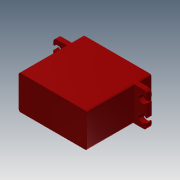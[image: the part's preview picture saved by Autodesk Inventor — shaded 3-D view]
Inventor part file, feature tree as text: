
AUTODESK INVENTOR PART (.ipt)
format: ipt  version: 2013 (Build 170138000, 138)  size: 210,432 bytes
history: native  units: mm
features: fillet x12, extrude x8, sketch x8, chamfer x1
ambient origin geometry x8: Origin, YZ Plane, XZ Plane, XY Plane, X Axis, Y Axis, Z Axis, Center Point
bodies: Solid1 (feature_tree)
feature tree (29):
  extrude  "Extrusion1"  Depth=7.4mm TaperAngle=0.0deg
  sketch  "Sketch2"  dims[d10=7.4mm d11=0.0mm d18=5.8mm d19=0.0mm]
  extrude  "Extrusion2"  Depth=5.8mm TaperAngle=0.0deg
  extrude  "Extrusion3"  Depth=4.0mm TaperAngle=0.0deg
  extrude  "Extrusion4"  Depth=2.0mm
  extrude  "Extrusion5"  Depth=2.0mm
  fillet  "Fillet1"  Radius=1.0mm
  fillet  "Fillet2"  Radius=1.0mm
  fillet  "Fillet3"  Radius=1.0mm
  fillet  "Fillet4"  Radius=1.0mm
  fillet  "Fillet5"  Radius=1.0mm
  fillet  "Fillet6"  Radius=1.0mm
  fillet  "Fillet7"  Radius=1.0mm
  fillet  "Fillet8"  Radius=1.0mm
  fillet  "Fillet9"  Radius=4.0mm
  fillet  "Fillet10"  Radius=3.0mm
  fillet  "Fillet11"  Radius=3.0mm
  fillet  "Fillet12"  [1 undecoded]
  extrude  "Extrusion6"  [1 undecoded]
  chamfer  "Chamfer3"  [1 undecoded]
  sketch  "Sketch7"
  sketch  "Sketch8"
  extrude  "Extrusion7"  [1 undecoded]
  extrude  "Extrusion8"  [1 undecoded]
  sketch  "Sketch1"  dims[d2=43.7mm d3=0.0mm d8=7.4mm d9=0.0mm]
  sketch  "Sketch3"  dims[d20=5.0mm d21=4.0mm d22=0.0mm]
  sketch  "Sketch4"  dims[d26=2.0mm d27=2.0mm]
  sketch  "Sketch5"  dims[d28=2.0mm d29=2.0mm d30=1.0mm d31=1.0mm d32=1.0mm d33=1.0mm d34=1.0mm d35=1.0mm d36=1.0mm d37=1.0mm d39=4.0mm d40=0.0mm]
  sketch  "Sketch6"  dims[d44=1.8mm d45=1.6mm d46=45.0deg d71=3.0mm d72=0.0mm d73=3.0mm d74=0.0mm]
note: 5 required parameter values undecoded (feature->parameter linkage not recoverable at this tier; creation-order binding heuristic only, values carry confidence <= 0.55)
